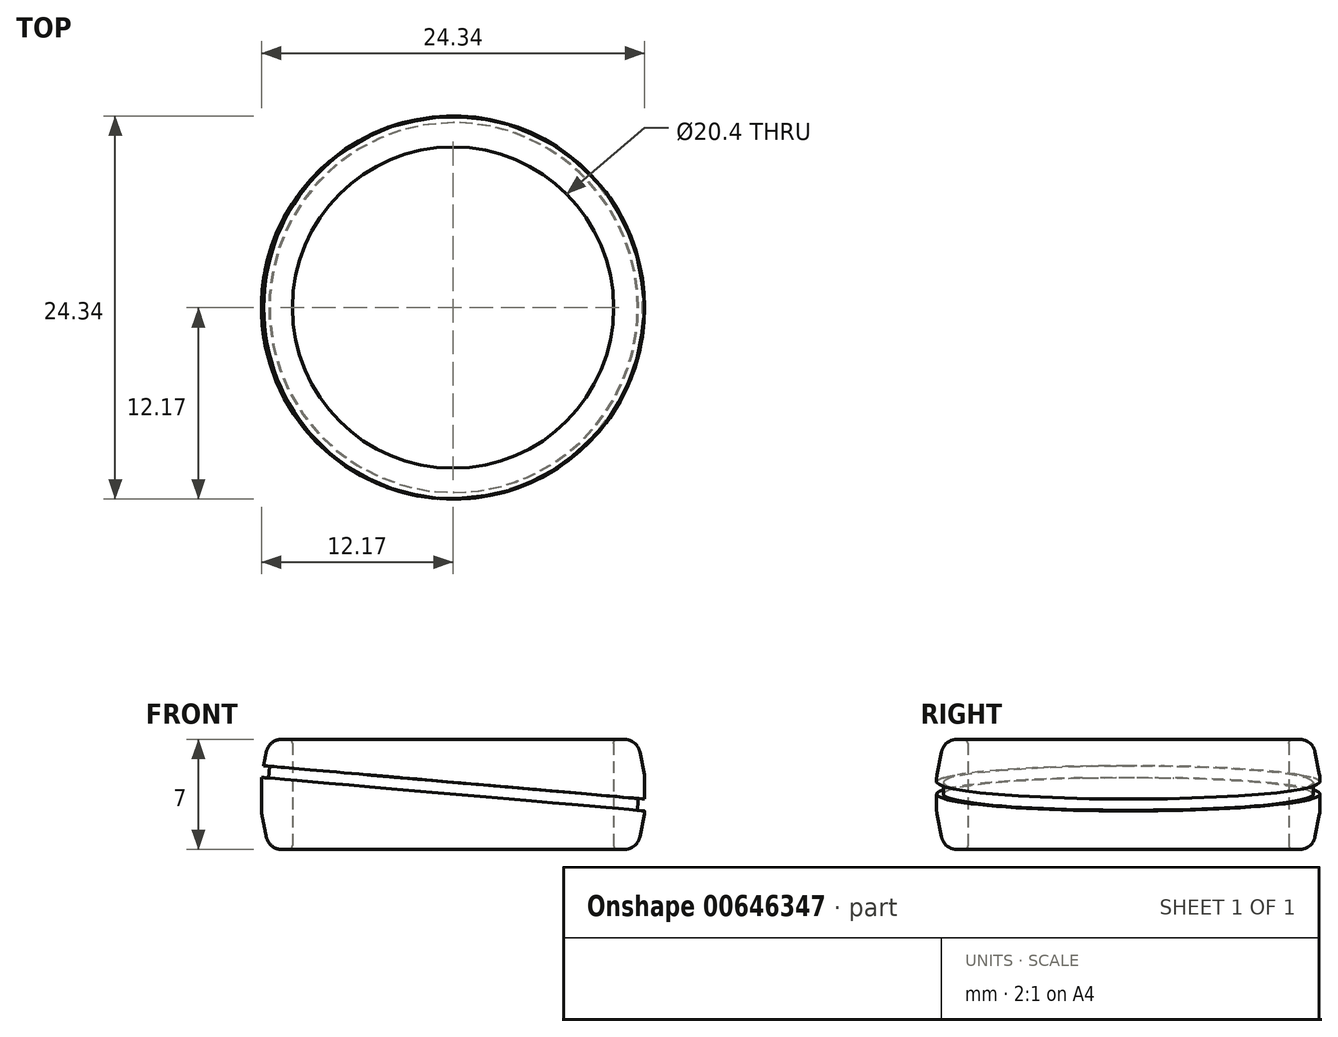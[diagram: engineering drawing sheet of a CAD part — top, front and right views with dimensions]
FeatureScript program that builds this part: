
annotation { "Feature Type Name" : "Feature", "Feature Type Description" : "" }
export const myFeature = defineFeature(function(context is Context, id is Id, definition is map)
    precondition{}
    {
        {
            var Q0;
            Q0=qCreatedBy(makeId("Front.planeOp"),FACE);
            var sketch = newSketch(context, id + "F0", { "sketchPlane" : qUnion([Q0])});
            skLineSegment(sketch, "E0", {"start": v(0, 0) * mm, "end": v(0, 3.25) * mm});
            skLineSegment(sketch, "E1", {"start": v(0.25, 3.5) * mm, "end": v(0.68, 3.5) * mm});
            skLineSegment(sketch, "E2", {"start": v(1.66, 2.7) * mm, "end": v(1.95, 1.25) * mm});
            skLineSegment(sketch, "E3", {"start": v(1.97, 1.05) * mm, "end": v(1.97, 0) * mm});
            skArc(sketch, "E4.filletArc", {"start": v(1.66, 2.7) * mm, "mid": v(1.31, 3.27) * mm, "end": v(0.68, 3.5) * mm});
            skPoint(sketch, "E5.visualSharp", {"position": v(1.97, 1.15) * mm});
            skArc(sketch, "E5.filletArc", {"start": v(1.97, 1.05) * mm, "mid": v(1.97, 1.15) * mm, "end": v(1.95, 1.25) * mm});
            skPoint(sketch, "E6.visualSharp", {"position": v(0, 3.5) * mm});
            skArc(sketch, "E6.filletArc", {"start": v(0.25, 3.5) * mm, "mid": v(0.07, 3.43) * mm, "end": v(0, 3.25) * mm});
            skLineSegment(sketch, "E7", {"start": v(0, 0) * mm, "end": v(1.97, 0) * mm, "construction": true});
            skArc(sketch, "E8.MirrorCS", {"start": v(1.97, -1.05) * mm, "mid": v(1.97, -1.15) * mm, "end": v(1.95, -1.25) * mm});
            skLineSegment(sketch, "E9.MirrorCS", {"start": v(0.25, -3.5) * mm, "end": v(0.68, -3.5) * mm});
            skArc(sketch, "E10.MirrorCS", {"start": v(0.25, -3.5) * mm, "mid": v(0.07, -3.43) * mm, "end": v(0, -3.25) * mm});
            skLineSegment(sketch, "E11.MirrorCS", {"start": v(0, 0) * mm, "end": v(0, -3.25) * mm});
            skPoint(sketch, "E12.MirrorP", {"position": v(0, -3.5) * mm});
            skLineSegment(sketch, "E13.MirrorCS", {"start": v(1.66, -2.7) * mm, "end": v(1.95, -1.25) * mm});
            skLineSegment(sketch, "E14.MirrorCS", {"start": v(1.97, -1.05) * mm, "end": v(1.97, 0) * mm});
            skPoint(sketch, "E15.MirrorP", {"position": v(1.97, -1.15) * mm});
            skArc(sketch, "E16.MirrorCS", {"start": v(1.66, -2.7) * mm, "mid": v(1.31, -3.27) * mm, "end": v(0.68, -3.5) * mm});
            skLineSegment(sketch, "E17", {"start": v(0, 0) * mm, "end": v(-10.2, 0) * mm, "construction": true});
            skLineSegment(sketch, "E18", {"start": v(-10.2, 0) * mm, "end": v(-10.2, 3.5) * mm, "construction": true});
            skSolve(sketch);
        }
        {
            var Q0;
            Q0=makeQuery(id+"F0.imprint","IMPRINT",FACE,{"disambiguationData":[TD([[makeQuery(id+"F0.imprint","IMPRINT",EDGE,{"derivedFrom":sQuery(id+"F0.wireOp",EDGE,"E0")}),-1.0]])]});
            var Q1;
            Q1=sQuery(id+"F0.wireOp",EDGE,"E18");
            revolve(context, id + "F1", {"entities" : qUnion([Q0]), "axis" : qUnion([Q1]), "revolveType" : RevolveType.FULL});
        }
        {
            var Q0;
            Q0=qCreatedBy(makeId("Top.planeOp"),FACE);
            var sketch = newSketch(context, id + "F2", { "sketchPlane" : qUnion([Q0])});
            skCircle(sketch, "E19", {"center": v(-10.08, 0) * mm, "radius": 18.15 * mm});
            skSolve(sketch);
        }
        {
            var Q0;
            Q0=qCreatedBy(makeId("Top.planeOp"),FACE);
            var sketch = newSketch(context, id + "F3", { "sketchPlane" : qUnion([Q0])});
            skCircle(sketch, "E20", {"center": v(-10.2, 0) * mm, "radius": 11.75 * mm});
            skSolve(sketch);
        }
        {
            var Q0;
            Q0=qCreatedBy(makeId("Top.planeOp"),FACE);
            var sketch = newSketch(context, id + "F4", { "sketchPlane" : qUnion([Q0])});
            skLineSegment(sketch, "E21", {"start": v(-10.02, 0) * mm, "end": v(-10.02, 34.58) * mm, "construction": true});
            skSolve(sketch);
        }
        {
            var Q0;
            Q0=makeQuery(id+"F3.imprint","IMPRINT",FACE,{"disambiguationData":[TD([[makeQuery(id+"F3.imprint","IMPRINT",EDGE,{"derivedFrom":sQuery(id+"F3.wireOp",EDGE,"E20")}),1.0]])]});
            var Q1;
            Q1=makeQuery(id+"F2.imprint","IMPRINT",FACE,{"disambiguationData":[TD([[makeQuery(id+"F2.imprint","IMPRINT",EDGE,{"derivedFrom":sQuery(id+"F2.wireOp",EDGE,"E19")}),1.0]])]});
            extrude(context, id + "F5", {"entities" : qUnion([Q0, Q1]), "depth" : .75 * mm, "offsetDistance" : 25 * mm});
        }
        {
            var Q0;
            Q0=makeQuery(id+"F5.opExtrude","SWEPT_BODY",BODY,{"disambiguationData":[OSD([sQuery(id+"F3.wireOp",EDGE,"E20")])]});
            var Q1;
            Q1=makeQuery(id+"F5.opExtrude","SWEPT_BODY",BODY,{"disambiguationData":[OSD([sQuery(id+"F2.wireOp",EDGE,"E19")])]});
            booleanBodies(context, id + "F6", {"operationType" : BooleanOperationType.SUBTRACTION, "tools" : qUnion([Q0]), "targets" : qUnion([Q1])});
        }
        {
            var Q0;
            Q0=makeQuery(id+"F5.opExtrude","SWEPT_BODY",BODY,{"disambiguationData":[OSD([sQuery(id+"F2.wireOp",EDGE,"E19")])]});
            var Q1;
            Q1=sQuery(id+"F4.wireOp",EDGE,"E21");
            transform(context, id + "F7", {"entities" : qUnion([Q0]), "transformType" : TransformType.ROTATION, "transformAxis" : qUnion([Q1]), "angle" : 5 * degree, "makeCopy" : false});
        }
        {
            var Q0;
            Q0=makeQuery(id+"F5.opExtrude","SWEPT_BODY",BODY,{"disambiguationData":[OSD([sQuery(id+"F2.wireOp",EDGE,"E19")])]});
            var Q1;
            Q1=makeQuery(id+"F1.opRevolve","SWEPT_BODY",BODY,{"disambiguationData":[OSD([sQuery(id+"F0.wireOp",EDGE,"E0"),sQuery(id+"F0.wireOp",EDGE,"E1"),sQuery(id+"F0.wireOp",EDGE,"E2"),sQuery(id+"F0.wireOp",EDGE,"E3"),sQuery(id+"F0.wireOp",EDGE,"E4.filletArc"),sQuery(id+"F0.wireOp",EDGE,"E5.filletArc"),sQuery(id+"F0.wireOp",EDGE,"E6.filletArc"),sQuery(id+"F0.wireOp",EDGE,"E8.MirrorCS"),sQuery(id+"F0.wireOp",EDGE,"E9.MirrorCS"),sQuery(id+"F0.wireOp",EDGE,"E10.MirrorCS"),sQuery(id+"F0.wireOp",EDGE,"E11.MirrorCS"),sQuery(id+"F0.wireOp",EDGE,"E13.MirrorCS"),sQuery(id+"F0.wireOp",EDGE,"E14.MirrorCS"),sQuery(id+"F0.wireOp",EDGE,"E16.MirrorCS")])]});
            booleanBodies(context, id + "F8", {"operationType" : BooleanOperationType.SUBTRACTION, "tools" : qUnion([Q0]), "targets" : qUnion([Q1])});
        }
    });
